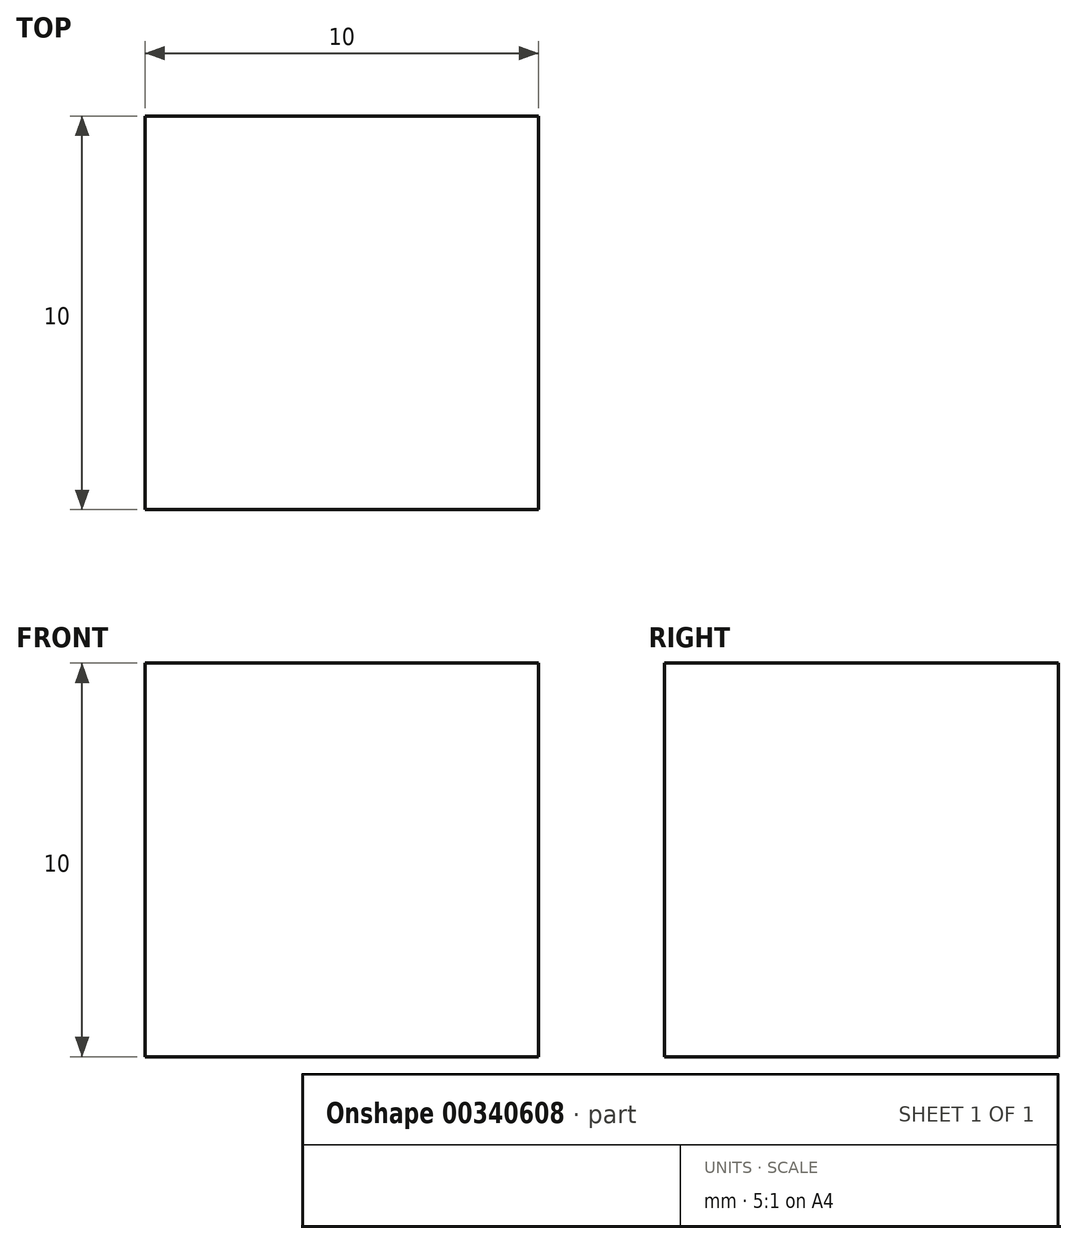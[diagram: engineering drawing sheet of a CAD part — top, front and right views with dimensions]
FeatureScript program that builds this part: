
annotation { "Feature Type Name" : "Feature", "Feature Type Description" : "" }
export const myFeature = defineFeature(function(context is Context, id is Id, definition is map)
    precondition{}
    {
        {
            var Q0;
            Q0=qCreatedBy(makeId("Top.planeOp"),FACE);
            var sketch = newSketch(context, id + "F0", { "sketchPlane" : qUnion([Q0])});
            skLineSegment(sketch, "E0.bottom", {"start": v(-5, -5) * mm, "end": v(5, -5) * mm});
            skLineSegment(sketch, "E0.top", {"start": v(-5, 5) * mm, "end": v(5, 5) * mm});
            skLineSegment(sketch, "E0.left", {"start": v(-5, -5) * mm, "end": v(-5, 5) * mm});
            skLineSegment(sketch, "E0.right", {"start": v(5, -5) * mm, "end": v(5, 5) * mm});
            skPoint(sketch, "E0.middle", {"position": v(0, 0) * mm});
            skSolve(sketch);
        }
        {
            var Q0;
            Q0=makeQuery(id+"F0.imprint","IMPRINT",FACE,{"disambiguationData":[TD([[makeQuery(id+"F0.imprint","IMPRINT",EDGE,{"derivedFrom":sQuery(id+"F0.wireOp",EDGE,"E0.bottom")}),1.0]])]});
            extrude(context, id + "F1", {"entities" : qUnion([Q0]), "depth" : 10 * mm});
        }
    });
